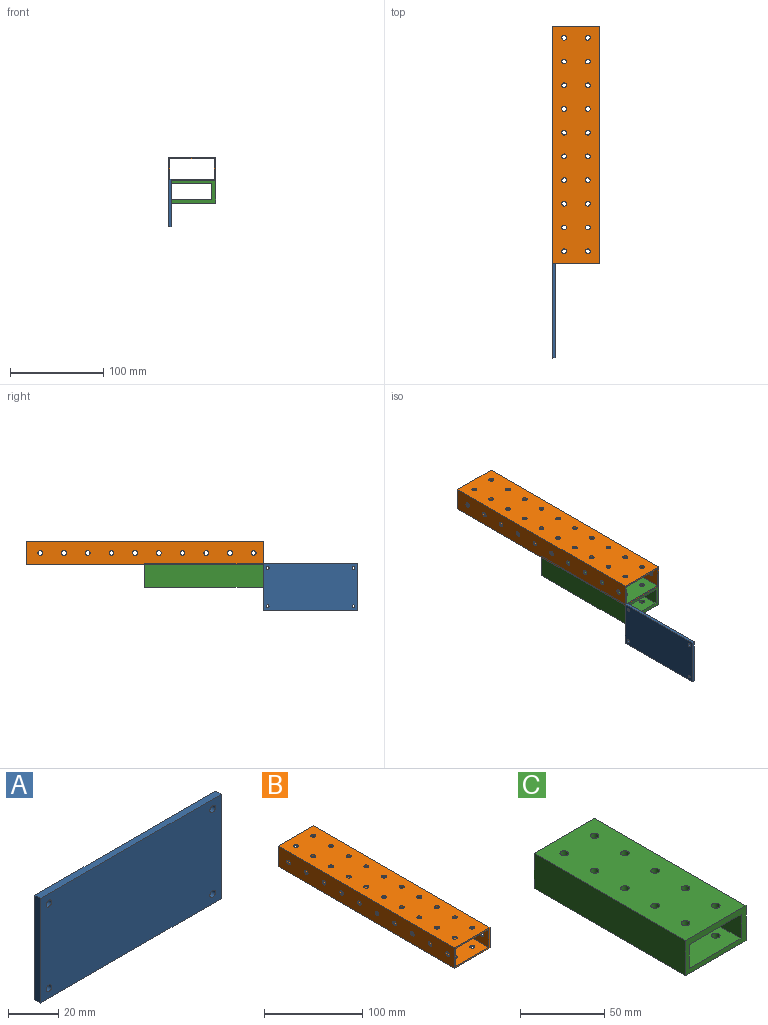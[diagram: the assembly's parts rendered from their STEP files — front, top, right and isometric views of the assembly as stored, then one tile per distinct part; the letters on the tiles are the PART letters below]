
ASSEMBLY  parts=3 mates=3
PART A: 10 faces, bbox 101.6x3.2x50.8 mm
  f0: plane 50.8x3.18mm, normal (-1,0,0), area 161.3mm2, adj f1,f3,f4,f5
  f1: plane 101.6x3.18mm, normal (0,0,-1), area 322.6mm2, adj f0,f2,f4,f5
  f2: plane 50.8x3.18mm, normal (1,0,0), area 161.3mm2, adj f1,f3,f4,f5
  f3: plane 101.6x3.18mm, normal (0,0,1), area 322.6mm2, adj f0,f2,f4,f5
  f4: plane 101.6x50.8mm, normal (0,-1,0), area 5129.6mm2, adj f0,f1,f2,f3,f6,f7,f8,f9
  f5: plane 101.6x50.8mm, normal (0,1,0), area 5129.6mm2, adj f0,f1,f2,f3,f6,f7,f8,f9
  f6: cylinder r=1.59mm len=3.18mm, axis (0,1,0), area 31.7mm2, adj f4,f5
  f7: cylinder r=1.59mm len=3.18mm, axis (0,1,0), area 31.7mm2, adj f4,f5
  f8: cylinder r=1.59mm len=3.18mm, axis (0,1,0), area 31.7mm2, adj f4,f5
  f9: cylinder r=1.59mm len=3.18mm, axis (0,1,0), area 31.7mm2, adj f4,f5
PART B: 70 faces, bbox 50.8x254x25.4 mm
  f0: plane 254x22.23mm, normal (1,0,0), area 5440.4mm2, adj f1,f7,f8,f9,f11,f13,f15,f17
  f1: plane 254x47.63mm, normal (0,0,-1), area 11687.3mm2, adj f0,f2,f8,f9,f31,f33,f35,f37
  f2: plane 254x22.23mm, normal (-1,0,0), area 5440.4mm2, adj f1,f7,f8,f9,f10,f12,f14,f16
  f3: plane 254x25.4mm, normal (-1,0,0), area 6246.9mm2, adj f4,f6,f8,f9,f11,f13,f15,f17
  f4: plane 254x50.8mm, normal (0,0,-1), area 12493.8mm2, adj f3,f5,f8,f9,f30,f32,f34,f36
  f5: plane 254x25.4mm, normal (1,0,0), area 6246.9mm2, adj f4,f6,f8,f9,f10,f12,f14,f16
  f6: plane 254x50.8mm, normal (0,0,1), area 12493.8mm2, adj f3,f5,f8,f9,f31,f33,f35,f37
  f7: plane 254x47.63mm, normal (0,0,1), area 11687.3mm2, adj f0,f2,f8,f9,f30,f32,f34,f36
  f8: plane 50.8x25.4mm, normal (0,-1,0), area 231.9mm2, adj f0,f1,f2,f3,f4,f5,f6,f7
  f9: plane 50.8x25.4mm, normal (0,1,0), area 231.9mm2, adj f0,f1,f2,f3,f4,f5,f6,f7
  f10: cylinder r=2.55mm len=5.11mm, axis (-1,0,0), area 25.5mm2, adj f2,f5
  f11: cylinder r=2.55mm len=5.11mm, axis (-1,0,0), area 25.5mm2, adj f0,f3
  f12: cylinder r=2.55mm len=5.11mm, axis (-1,0,0), area 25.5mm2, adj f2,f5
  f13: cylinder r=2.55mm len=5.11mm, axis (-1,0,0), area 25.5mm2, adj f0,f3
  f14: cylinder r=2.55mm len=5.11mm, axis (-1,0,0), area 25.5mm2, adj f2,f5
  f15: cylinder r=2.55mm len=5.11mm, axis (-1,0,0), area 25.5mm2, adj f0,f3
  f16: cylinder r=2.55mm len=5.11mm, axis (-1,0,0), area 25.5mm2, adj f2,f5
  f17: cylinder r=2.55mm len=5.11mm, axis (-1,0,0), area 25.5mm2, adj f0,f3
  f18: cylinder r=2.55mm len=5.11mm, axis (-1,0,0), area 25.5mm2, adj f2,f5
  f19: cylinder r=2.55mm len=5.11mm, axis (-1,0,0), area 25.5mm2, adj f0,f3
  f20: cylinder r=2.55mm len=5.11mm, axis (-1,0,0), area 25.5mm2, adj f2,f5
  f21: cylinder r=2.55mm len=5.11mm, axis (-1,0,0), area 25.5mm2, adj f0,f3
  f22: cylinder r=2.55mm len=5.11mm, axis (-1,0,0), area 25.5mm2, adj f2,f5
  f23: cylinder r=2.55mm len=5.11mm, axis (-1,0,0), area 25.5mm2, adj f0,f3
  f24: cylinder r=2.55mm len=5.11mm, axis (-1,0,0), area 25.5mm2, adj f2,f5
  f25: cylinder r=2.55mm len=5.11mm, axis (-1,0,0), area 25.5mm2, adj f0,f3
  f26: cylinder r=2.55mm len=5.11mm, axis (-1,0,0), area 25.5mm2, adj f2,f5
  f27: cylinder r=2.55mm len=5.11mm, axis (-1,0,0), area 25.5mm2, adj f0,f3
  f28: cylinder r=2.55mm len=5.11mm, axis (-1,0,0), area 25.5mm2, adj f2,f5
  f29: cylinder r=2.55mm len=5.11mm, axis (-1,0,0), area 25.5mm2, adj f0,f3
  f30: cylinder r=2.55mm len=5.11mm, axis (0,0,-1), area 25.5mm2, adj f4,f7
  f31: cylinder r=2.55mm len=5.11mm, axis (0,0,-1), area 25.5mm2, adj f1,f6
  f32: cylinder r=2.55mm len=5.11mm, axis (0,0,-1), area 25.5mm2, adj f4,f7
  f33: cylinder r=2.55mm len=5.11mm, axis (0,0,-1), area 25.5mm2, adj f1,f6
  f34: cylinder r=2.55mm len=5.11mm, axis (0,0,-1), area 25.5mm2, adj f4,f7
  f35: cylinder r=2.55mm len=5.11mm, axis (0,0,-1), area 25.5mm2, adj f1,f6
  f36: cylinder r=2.55mm len=5.11mm, axis (0,0,-1), area 25.5mm2, adj f4,f7
  f37: cylinder r=2.55mm len=5.11mm, axis (0,0,-1), area 25.5mm2, adj f1,f6
  f38: cylinder r=2.55mm len=5.11mm, axis (0,0,-1), area 25.5mm2, adj f4,f7
  f39: cylinder r=2.55mm len=5.11mm, axis (0,0,-1), area 25.5mm2, adj f1,f6
  f40: cylinder r=2.55mm len=5.11mm, axis (0,0,-1), area 25.5mm2, adj f4,f7
  f41: cylinder r=2.55mm len=5.11mm, axis (0,0,-1), area 25.5mm2, adj f1,f6
  f42: cylinder r=2.55mm len=5.11mm, axis (0,0,-1), area 25.5mm2, adj f4,f7
  f43: cylinder r=2.55mm len=5.11mm, axis (0,0,-1), area 25.5mm2, adj f1,f6
  f44: cylinder r=2.55mm len=5.11mm, axis (0,0,-1), area 25.5mm2, adj f4,f7
  f45: cylinder r=2.55mm len=5.11mm, axis (0,0,-1), area 25.5mm2, adj f1,f6
  f46: cylinder r=2.55mm len=5.11mm, axis (0,0,-1), area 25.5mm2, adj f4,f7
  f47: cylinder r=2.55mm len=5.11mm, axis (0,0,-1), area 25.5mm2, adj f1,f6
  f48: cylinder r=2.55mm len=5.11mm, axis (0,0,-1), area 25.5mm2, adj f4,f7
  f49: cylinder r=2.55mm len=5.11mm, axis (0,0,-1), area 25.5mm2, adj f1,f6
  f50: cylinder r=2.55mm len=5.11mm, axis (0,0,-1), area 25.5mm2, adj f4,f7
  f51: cylinder r=2.55mm len=5.11mm, axis (0,0,-1), area 25.5mm2, adj f1,f6
  f52: cylinder r=2.55mm len=5.11mm, axis (0,0,-1), area 25.5mm2, adj f4,f7
  f53: cylinder r=2.55mm len=5.11mm, axis (0,0,-1), area 25.5mm2, adj f1,f6
  f54: cylinder r=2.55mm len=5.11mm, axis (0,0,-1), area 25.5mm2, adj f4,f7
  f55: cylinder r=2.55mm len=5.11mm, axis (0,0,-1), area 25.5mm2, adj f1,f6
  f56: cylinder r=2.55mm len=5.11mm, axis (0,0,-1), area 25.5mm2, adj f4,f7
  f57: cylinder r=2.55mm len=5.11mm, axis (0,0,-1), area 25.5mm2, adj f1,f6
  f58: cylinder r=2.55mm len=5.11mm, axis (0,0,-1), area 25.5mm2, adj f4,f7
  f59: cylinder r=2.55mm len=5.11mm, axis (0,0,-1), area 25.5mm2, adj f1,f6
  f60: cylinder r=2.55mm len=5.11mm, axis (0,0,-1), area 25.5mm2, adj f4,f7
  f61: cylinder r=2.55mm len=5.11mm, axis (0,0,-1), area 25.5mm2, adj f1,f6
  f62: cylinder r=2.55mm len=5.11mm, axis (0,0,-1), area 25.5mm2, adj f4,f7
  f63: cylinder r=2.55mm len=5.11mm, axis (0,0,-1), area 25.5mm2, adj f1,f6
  f64: cylinder r=2.55mm len=5.11mm, axis (0,0,-1), area 25.5mm2, adj f4,f7
  f65: cylinder r=2.55mm len=5.11mm, axis (0,0,-1), area 25.5mm2, adj f1,f6
  f66: cylinder r=2.55mm len=5.11mm, axis (0,0,-1), area 25.5mm2, adj f4,f7
  f67: cylinder r=2.55mm len=5.11mm, axis (0,0,-1), area 25.5mm2, adj f1,f6
  f68: cylinder r=2.55mm len=5.11mm, axis (0,0,-1), area 25.5mm2, adj f4,f7
  f69: cylinder r=2.55mm len=5.11mm, axis (0,0,-1), area 25.5mm2, adj f1,f6
PART C: 30 faces, bbox 50.8x127x25.4 mm
  f0: plane 50.8x25.4mm, normal (0,-1,0), area 536mm2, adj f2,f3,f4,f5,f6,f7,f8,f9
  f1: plane 50.8x25.4mm, normal (0,1,0), area 536mm2, adj f2,f3,f4,f5,f6,f7,f8,f9
  f2: plane 127x50.8mm, normal (0,0,1), area 6246.9mm2, adj f0,f1,f3,f5,f11,f13,f15,f17
  f3: plane 127x25.4mm, normal (-1,0,0), area 3225.8mm2, adj f0,f1,f2,f4
  f4: plane 127x50.8mm, normal (0,0,-1), area 6246.9mm2, adj f0,f1,f3,f5,f10,f12,f14,f16
  f5: plane 127x25.4mm, normal (1,0,0), area 3225.8mm2, adj f0,f1,f2,f4
  f6: plane 127x43.51mm, normal (0,0,-1), area 5321.5mm2, adj f0,f1,f7,f9,f11,f13,f15,f17
  f7: plane 127x17.33mm, normal (1,0,0), area 2201.5mm2, adj f0,f1,f6,f8
  f8: plane 127x43.51mm, normal (0,0,1), area 5321.5mm2, adj f0,f1,f7,f9,f10,f12,f14,f16
  f9: plane 127x17.33mm, normal (-1,0,0), area 2201.5mm2, adj f0,f1,f6,f8
  f10: cylinder r=2.55mm len=5.11mm, axis (0,0,1), area 58.8mm2, adj f4,f8
  f11: cylinder r=2.55mm len=5.11mm, axis (0,0,1), area 70.5mm2, adj f2,f6
  f12: cylinder r=2.55mm len=5.11mm, axis (0,0,1), area 58.8mm2, adj f4,f8
  f13: cylinder r=2.55mm len=5.11mm, axis (0,0,1), area 70.5mm2, adj f2,f6
  f14: cylinder r=2.55mm len=5.11mm, axis (0,0,1), area 58.8mm2, adj f4,f8
  f15: cylinder r=2.55mm len=5.11mm, axis (0,0,1), area 70.5mm2, adj f2,f6
  f16: cylinder r=2.55mm len=5.11mm, axis (0,0,1), area 58.8mm2, adj f4,f8
  f17: cylinder r=2.55mm len=5.11mm, axis (0,0,1), area 70.5mm2, adj f2,f6
  f18: cylinder r=2.55mm len=5.11mm, axis (0,0,1), area 58.8mm2, adj f4,f8
  f19: cylinder r=2.55mm len=5.11mm, axis (0,0,1), area 70.5mm2, adj f2,f6
  f20: cylinder r=2.55mm len=5.11mm, axis (0,0,1), area 58.8mm2, adj f4,f8
  f21: cylinder r=2.55mm len=5.11mm, axis (0,0,1), area 70.5mm2, adj f2,f6
  f22: cylinder r=2.55mm len=5.11mm, axis (0,0,1), area 58.8mm2, adj f4,f8
  f23: cylinder r=2.55mm len=5.11mm, axis (0,0,1), area 70.5mm2, adj f2,f6
  f24: cylinder r=2.55mm len=5.11mm, axis (0,0,1), area 58.8mm2, adj f4,f8
  f25: cylinder r=2.55mm len=5.11mm, axis (0,0,1), area 70.5mm2, adj f2,f6
  f26: cylinder r=2.55mm len=5.11mm, axis (0,0,1), area 58.8mm2, adj f4,f8
  f27: cylinder r=2.55mm len=5.11mm, axis (0,0,1), area 70.5mm2, adj f2,f6
  f28: cylinder r=2.55mm len=5.11mm, axis (0,0,1), area 58.8mm2, adj f4,f8
  f29: cylinder r=2.55mm len=5.11mm, axis (0,0,1), area 70.5mm2, adj f2,f6
PLACE A rot(axis=(0,0,1),90deg) t=(-40.47,-162.41,-31.55)mm
PLACE B t=(-24.53,159.39,-3.46)mm
PLACE C t=(-36.24,32.39,-41.08)mm
MATE fastened B.f68 <-> C.f10  axis (0,0,1) through (-27.77,-81.91,-20.92)mm
MATE fastened C.f5 <-> C.f5  axis (1,0,0) through (10.33,-94.61,-20.92)mm
MATE fastened A.f3 <-> C.f2  axis (0,0,1) through (-40.47,-94.61,-20.92)mm
